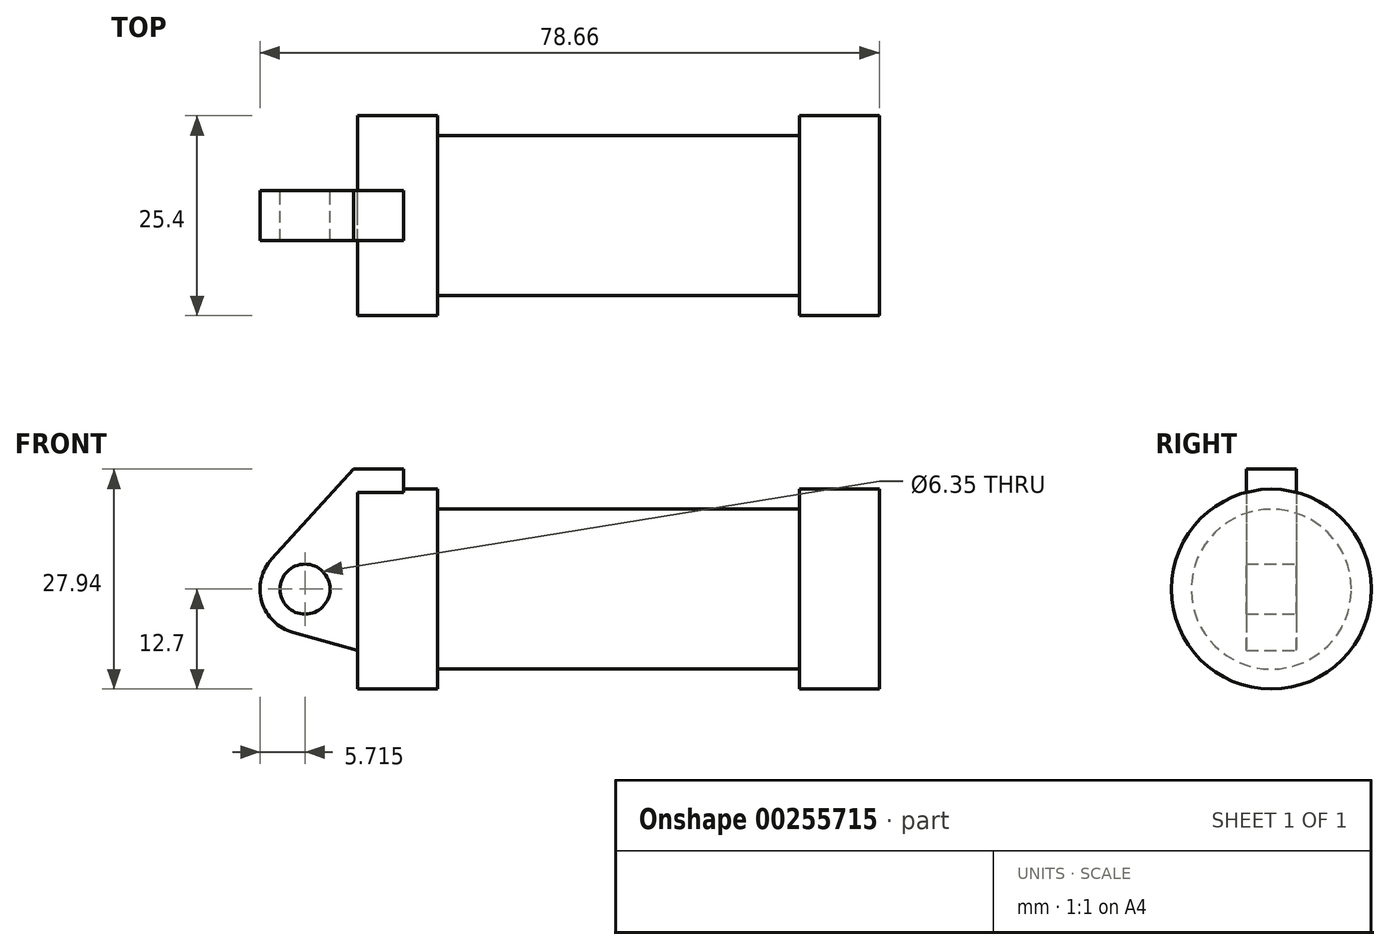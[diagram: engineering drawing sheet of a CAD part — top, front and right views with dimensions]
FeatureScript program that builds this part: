
annotation { "Feature Type Name" : "Feature", "Feature Type Description" : "" }
export const myFeature = defineFeature(function(context is Context, id is Id, definition is map)
    precondition{}
    {
        {
            var Q0;
            Q0=qCreatedBy(makeId("Front.planeOp"),FACE);
            var sketch = newSketch(context, id + "F0", { "sketchPlane" : qUnion([Q0])});
            skLineSegment(sketch, "E0", {"start": v(0, 0) * mm, "end": v(0, 12.7) * mm});
            skLineSegment(sketch, "E1", {"start": v(0, 12.7) * mm, "end": v(10.16, 12.7) * mm});
            skLineSegment(sketch, "E2", {"start": v(10.16, 12.7) * mm, "end": v(10.16, 10.16) * mm});
            skLineSegment(sketch, "E3", {"start": v(10.16, 10.16) * mm, "end": v(56.13, 10.16) * mm});
            skLineSegment(sketch, "E4", {"start": v(56.13, 10.16) * mm, "end": v(56.13, 12.7) * mm});
            skLineSegment(sketch, "E5", {"start": v(56.13, 12.7) * mm, "end": v(66.3, 12.7) * mm});
            skLineSegment(sketch, "E6", {"start": v(66.3, 12.7) * mm, "end": v(66.3, 0) * mm});
            skLineSegment(sketch, "E7", {"start": v(66.3, 0) * mm, "end": v(0, 0) * mm});
            skLineSegment(sketch, "E8", {"start": v(5.84, 15.24) * mm, "end": v(-0.5, 15.24) * mm});
            skLineSegment(sketch, "E9", {"start": v(-0.5, 15.24) * mm, "end": v(-10.88, 3.85) * mm});
            skLineSegment(sketch, "E10", {"start": v(0, 0) * mm, "end": v(-6.65, 0) * mm});
            skCircle(sketch, "E11", {"center": v(-6.65, 0) * mm, "radius": 5.72 * mm});
            skCircle(sketch, "E12", {"center": v(-6.65, 0) * mm, "radius": 3.18 * mm});
            skLineSegment(sketch, "E13", {"start": v(5.84, 15.24) * mm, "end": v(5.84, -9.4) * mm});
            skLineSegment(sketch, "E14", {"start": v(5.84, -9.4) * mm, "end": v(-8.18, -5.5) * mm});
            skSolve(sketch);
        }
        {
            var Q0;
            {var subQ0=sQuery(id+"F0.wireOp",EDGE,"E2");Q0=makeQuery(id+"F0.imprint","IMPRINT",FACE,{"disambiguationData":[TD([[makeQuery(id+"F0.imprint","IMPRINT",EDGE,{"derivedFrom":subQ0}),-1.0]])]});}
            var Q1;
            {var subQ0=sQuery(id+"F0.wireOp",EDGE,"E0");Q1=makeQuery(id+"F0.imprint","IMPRINT",FACE,{"disambiguationData":[TD([[makeQuery(id+"F0.imprint","IMPRINT",EDGE,{"derivedFrom":subQ0}),-1.0]])]});}
            var Q2;
            Q2=sQuery(id+"F0.wireOp",EDGE,"E7");
            revolve(context, id + "F1", {"entities" : qUnion([Q0, Q1]), "axis" : qUnion([Q2]), "revolveType" : RevolveType.FULL});
        }
        {
            var Q0;
            {var subQ3=sQuery(id+"F0.wireOp",EDGE,"E0");Q0=makeQuery(id+"F0.imprint","IMPRINT",FACE,{"disambiguationData":[TD([[makeQuery(id+"F0.imprint","IMPRINT",EDGE,{"derivedFrom":subQ3}),1.0]])]});}
            var Q1;
            {var subQ0=sQuery(id+"F0.wireOp",EDGE,"E14");Q1=makeQuery(id+"F0.imprint","IMPRINT",FACE,{"disambiguationData":[TD([[makeQuery(id+"F0.imprint","IMPRINT",EDGE,{"derivedFrom":subQ0}),-1.0]])]});}
            var Q2;
            {var subQ4=sQuery(id+"F0.wireOp",EDGE,"E12");Q2=makeQuery(id+"F0.imprint","IMPRINT",FACE,{"disambiguationData":[TD([[makeQuery(id+"F0.imprint","IMPRINT",EDGE,{"derivedFrom":subQ4}),-1.0]])]});}
            var Q3;
            {var subQ0=sQuery(id+"F0.wireOp",EDGE,"E0");Q3=makeQuery(id+"F0.imprint","IMPRINT",FACE,{"disambiguationData":[TD([[makeQuery(id+"F0.imprint","IMPRINT",EDGE,{"derivedFrom":subQ0}),-1.0]])]});}
            extrude(context, id + "F2", {"entities" : qUnion([Q0, Q1, Q2, Q3]), "operationType" : NewBodyOperationType.ADD, "depth" : 6.35 * mm, "hasSecondDirection" : true, "secondDirectionOppositeDirection" : true, "secondDirectionDepth" : 6.35 * mm, "symmetric" : true});
        }
    });
